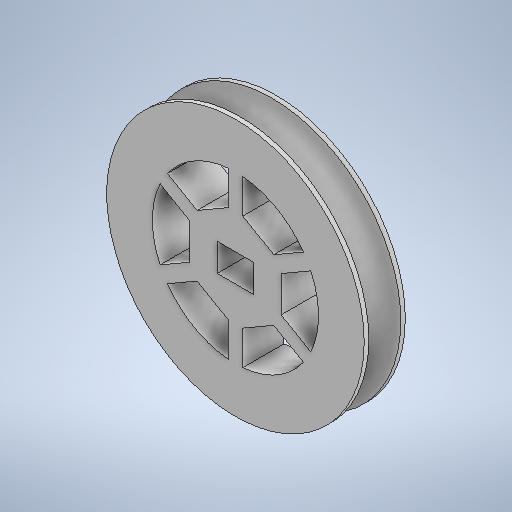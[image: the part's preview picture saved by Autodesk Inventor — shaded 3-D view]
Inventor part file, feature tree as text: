
AUTODESK INVENTOR PART (.ipt)
format: ipt  version: 2025.3 (Build 293356030, 356C)  size: 315,904 bytes
history: native  units: mm
features: sketch x4, extrude x3, other x1, pattern_circular x1
ambient origin geometry x8: Origin, YZ Plane, XZ Plane, XY Plane, X Axis, Y Axis, Z Axis, Center Point
bodies: Body1 (feature_tree)
feature tree (9):
  other  "ソリッド1"
  extrude  "ハブ"  Depth=5.0mm
  extrude  "スポーク"  TaperAngle=90.0deg  [1 undecoded]
  pattern_circular  "円形状パターン1"  [2 undecoded]
  extrude  "軸穴"  Depth=10.0mm TaperAngle=0.0deg
  sketch  "スケッチ1"
  sketch  "スケッチ3"
  sketch  "スケッチ4"
  sketch  "スケッチ5"
note: 3 required parameter values undecoded (feature->parameter linkage not recoverable at this tier; creation-order binding heuristic only, values carry confidence <= 0.55)
